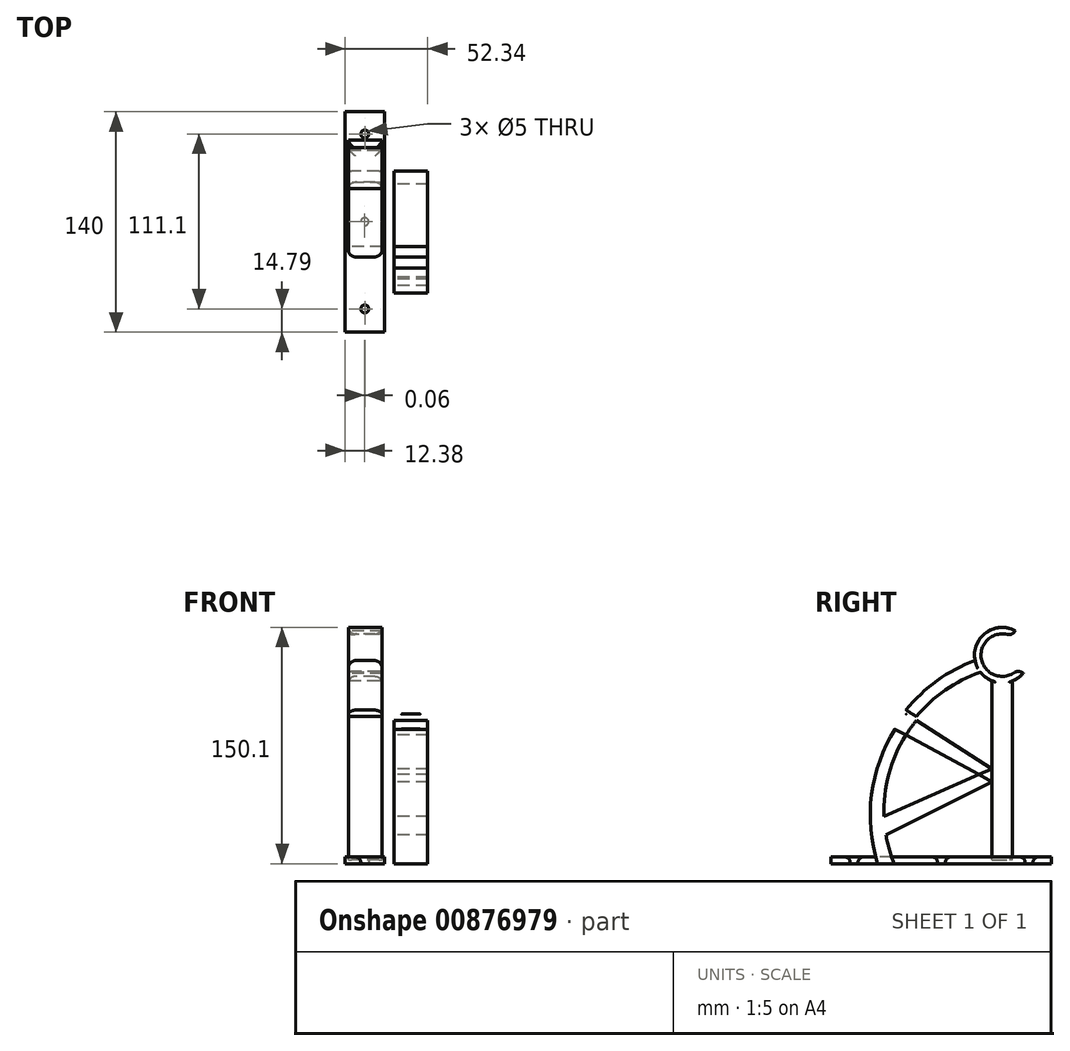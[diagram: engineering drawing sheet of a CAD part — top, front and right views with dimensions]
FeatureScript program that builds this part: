
annotation { "Feature Type Name" : "Feature", "Feature Type Description" : "" }
export const myFeature = defineFeature(function(context is Context, id is Id, definition is map)
    precondition{}
    {
        {
            var Q0;
            Q0=qCreatedBy(makeId("Top.planeOp"),FACE);
            var sketch = newSketch(context, id + "F0", { "sketchPlane" : qUnion([Q0])});
            skLineSegment(sketch, "E0.bottom", {"start": v(-31.04, 63.14) * mm, "end": v(-6.17, 63.14) * mm});
            skLineSegment(sketch, "E0.top", {"start": v(-31.04, -76.86) * mm, "end": v(-6.17, -76.86) * mm});
            skLineSegment(sketch, "E0.left", {"start": v(-31.04, 63.14) * mm, "end": v(-31.04, -76.86) * mm});
            skLineSegment(sketch, "E0.right", {"start": v(-6.17, 63.14) * mm, "end": v(-6.17, -76.86) * mm});
            skLineSegment(sketch, "E1", {"start": v(-18.6, 63.14) * mm, "end": v(-18.6, -76.86) * mm});
            skCircle(sketch, "E2", {"center": v(-18.6, 49.03) * mm, "radius": 2.5 * mm});
            skLineSegment(sketch, "E3.bottom", {"start": v(-27.13, 25.15) * mm, "end": v(-10.08, 25.15) * mm});
            skLineSegment(sketch, "E3.top", {"start": v(-27.13, 35.3) * mm, "end": v(-10.08, 35.3) * mm});
            skLineSegment(sketch, "E3.left", {"start": v(-27.13, 25.15) * mm, "end": v(-27.13, 35.3) * mm});
            skLineSegment(sketch, "E3.right", {"start": v(-10.08, 25.15) * mm, "end": v(-10.08, 35.3) * mm});
            skPoint(sketch, "E3.middle", {"position": v(-18.6, 30.23) * mm});
            skCircle(sketch, "E4", {"center": v(-18.6, -62.07) * mm, "radius": 2.5 * mm});
            skLineSegment(sketch, "E5.bottom", {"start": v(-27.13, -47.05) * mm, "end": v(-10.08, -47.05) * mm});
            skLineSegment(sketch, "E5.top", {"start": v(-27.13, -36.9) * mm, "end": v(-10.08, -36.9) * mm});
            skLineSegment(sketch, "E5.left", {"start": v(-27.13, -47.05) * mm, "end": v(-27.13, -36.9) * mm});
            skLineSegment(sketch, "E5.right", {"start": v(-10.08, -47.05) * mm, "end": v(-10.08, -36.9) * mm});
            skPoint(sketch, "E5.middle", {"position": v(-18.6, -41.97) * mm});
            skCircle(sketch, "E6", {"center": v(-18.66, -6.6) * mm, "radius": 2.5 * mm});
            skSolve(sketch);
        }
        {
            var Q0;
            Q0=qCreatedBy(makeId("Right.planeOp"),FACE);
            var sketch = newSketch(context, id + "F1", { "sketchPlane" : qUnion([Q0])});
            skLineSegment(sketch, "E7.bottom", {"start": v(25.47, 0) * mm, "end": v(38.53, 0) * mm});
            skLineSegment(sketch, "E7.top", {"start": v(25.47, 130) * mm, "end": v(38.53, 130) * mm});
            skLineSegment(sketch, "E7.left", {"start": v(25.47, 0) * mm, "end": v(25.47, 130) * mm});
            skLineSegment(sketch, "E7.right", {"start": v(38.53, 0) * mm, "end": v(38.53, 130) * mm});
            skArc(sketch, "E8", {"start": v(25.47, 130) * mm, "mid": v(-38.86, 80.66) * mm, "end": v(-47.12, 0) * mm});
            skArc(sketch, "E9", {"start": v(25.47, 121.23) * mm, "mid": v(-33.16, 74.74) * mm, "end": v(-36.67, 0) * mm});
            skLineSegment(sketch, "E10", {"start": v(-47.12, 0) * mm, "end": v(-36.67, 0) * mm});
            skPoint(sketch, "E11.centerSnap0", {"position": v(32, 130) * mm});
            skLineSegment(sketch, "E12.left", {"start": v(25.47, 52.07) * mm, "end": v(25.47, 60.27) * mm});
            skCircle(sketch, "E13", {"center": v(32, 130) * mm, "radius": 13.5 * mm});
            skCircle(sketch, "E14", {"center": v(32, 130) * mm, "radius": 17.6 * mm});
            skArc(sketch, "E15", {"start": v(57.75, 150.75) * mm, "mid": v(36, 132.31) * mm, "end": v(60.85, 118.33) * mm});
            skLineSegment(sketch, "E16", {"start": v(25.47, 52.07) * mm, "end": v(-50.48, 14.07) * mm});
            skLineSegment(sketch, "E17", {"start": v(-50.48, 14.07) * mm, "end": v(-51.75, 26.23) * mm});
            skLineSegment(sketch, "E18", {"start": v(-51.75, 26.23) * mm, "end": v(25.47, 60.27) * mm});
            skLineSegment(sketch, "E19", {"start": v(25.47, 52.07) * mm, "end": v(-36.03, 85.43) * mm});
            skLineSegment(sketch, "E20", {"start": v(-36.03, 85.43) * mm, "end": v(-29.09, 95.12) * mm});
            skLineSegment(sketch, "E21", {"start": v(-29.09, 95.12) * mm, "end": v(25.47, 60.27) * mm});
            skSolve(sketch);
        }
        {
            var Q0;
            {var subQ20=sQuery(id+"F0.wireOp",EDGE,"E0.left");Q0=makeQuery(id+"F0.imprint","IMPRINT",FACE,{"disambiguationData":[TD([[makeQuery(id+"F0.imprint","IMPRINT",EDGE,{"derivedFrom":subQ20}),1.0]])]});}
            var Q1;
            {var subQ13=sQuery(id+"F0.wireOp",EDGE,"E0.right");Q1=makeQuery(id+"F0.imprint","IMPRINT",FACE,{"disambiguationData":[TD([[makeQuery(id+"F0.imprint","IMPRINT",EDGE,{"derivedFrom":subQ13}),-1.0]])]});}
            var Q2;
            {var subQ5=sQuery(id+"F0.wireOp",EDGE,"E3.right");Q2=makeQuery(id+"F0.imprint","IMPRINT",FACE,{"disambiguationData":[TD([[makeQuery(id+"F0.imprint","IMPRINT",EDGE,{"derivedFrom":subQ5}),1.0]])]});}
            var Q3;
            {var subQ5=sQuery(id+"F0.wireOp",EDGE,"E3.left");Q3=makeQuery(id+"F0.imprint","IMPRINT",FACE,{"disambiguationData":[TD([[makeQuery(id+"F0.imprint","IMPRINT",EDGE,{"derivedFrom":subQ5}),-1.0]])]});}
            var Q4;
            {var subQ5=sQuery(id+"F0.wireOp",EDGE,"E5.left");Q4=makeQuery(id+"F0.imprint","IMPRINT",FACE,{"disambiguationData":[TD([[makeQuery(id+"F0.imprint","IMPRINT",EDGE,{"derivedFrom":subQ5}),-1.0]])]});}
            var Q5;
            {var subQ5=sQuery(id+"F0.wireOp",EDGE,"E5.right");Q5=makeQuery(id+"F0.imprint","IMPRINT",FACE,{"disambiguationData":[TD([[makeQuery(id+"F0.imprint","IMPRINT",EDGE,{"derivedFrom":subQ5}),1.0]])]});}
            extrude(context, id + "F2", {"entities" : qUnion([Q0, Q1, Q2, Q3, Q4, Q5]), "depth" : 4.3 * mm, "offsetDistance" : 25 * mm});
        }
        {
            var Q0;
            {var subQ0=sQuery(id+"F1.wireOp",EDGE,"E21");var subQ1=sQuery(id+"F1.wireOp",EDGE,"E9");var subQ2=makeQuery(id+"F1.imprint","INTERSECT",VERTEX,{"derivedFrom":[subQ1,subQ0]});Q0=makeQuery(id+"F1.imprint","IMPRINT",FACE,{"disambiguationData":[TD([[makeQuery(id+"F1.imprint","IMPRINT",EDGE,{"disambiguationData":[TD([[subQ2,-1.0]])],"derivedFrom":subQ1}),1.0]])]});}
            var Q1;
            {var subQ0=sQuery(id+"F1.wireOp",EDGE,"E16");var subQ1=sQuery(id+"F1.wireOp",EDGE,"E9");var subQ2=makeQuery(id+"F1.imprint","INTERSECT",VERTEX,{"derivedFrom":[subQ1,subQ0]});Q1=makeQuery(id+"F1.imprint","IMPRINT",FACE,{"disambiguationData":[TD([[makeQuery(id+"F1.imprint","IMPRINT",EDGE,{"disambiguationData":[TD([[subQ2,1.0]])],"derivedFrom":subQ1}),1.0]])]});}
            var Q2;
            {var subQ0=sQuery(id+"F1.wireOp",EDGE,"E12.left");Q2=makeQuery(id+"F1.imprint","IMPRINT",FACE,{"disambiguationData":[TD([[makeQuery(id+"F1.imprint","IMPRINT",EDGE,{"derivedFrom":subQ0}),1.0]])]});}
            var Q3;
            {var subQ6=sQuery(id+"F1.wireOp",EDGE,"E7.bottom");Q3=makeQuery(id+"F1.imprint","IMPRINT",FACE,{"disambiguationData":[TD([[makeQuery(id+"F1.imprint","IMPRINT",EDGE,{"derivedFrom":subQ6}),1.0]])]});}
            var Q4;
            {var subQ3=sQuery(id+"F1.wireOp",EDGE,"E19");var subQ5=sQuery(id+"F1.wireOp",EDGE,"E9");var subQ6=makeQuery(id+"F1.imprint","INTERSECT",VERTEX,{"derivedFrom":[subQ5,subQ3]});Q4=makeQuery(id+"F1.imprint","IMPRINT",FACE,{"disambiguationData":[TD([[makeQuery(id+"F1.imprint","IMPRINT",EDGE,{"disambiguationData":[TD([[subQ6,-1.0]])],"derivedFrom":subQ5}),-1.0]])]});}
            var Q5;
            {var subQ5=sQuery(id+"F1.wireOp",EDGE,"E17");Q5=makeQuery(id+"F1.imprint","IMPRINT",FACE,{"disambiguationData":[TD([[makeQuery(id+"F1.imprint","IMPRINT",EDGE,{"derivedFrom":subQ5}),-1.0]])]});}
            var Q6;
            {var subQ0=sQuery(id+"F1.wireOp",EDGE,"E10");Q6=makeQuery(id+"F1.imprint","IMPRINT",FACE,{"disambiguationData":[TD([[makeQuery(id+"F1.imprint","IMPRINT",EDGE,{"derivedFrom":subQ0}),1.0]])]});}
            var Q7;
            {var subQ5=sQuery(id+"F1.wireOp",EDGE,"E20");Q7=makeQuery(id+"F1.imprint","IMPRINT",FACE,{"disambiguationData":[TD([[makeQuery(id+"F1.imprint","IMPRINT",EDGE,{"derivedFrom":subQ5}),-1.0]])]});}
            var Q8;
            {var subQ3=sQuery(id+"F1.wireOp",EDGE,"E14");var subQ5=sQuery(id+"F1.wireOp",EDGE,"E9");var subQ6=makeQuery(id+"F1.imprint","INTERSECT",VERTEX,{"derivedFrom":[subQ5,subQ3]});Q8=makeQuery(id+"F1.imprint","IMPRINT",FACE,{"disambiguationData":[TD([[makeQuery(id+"F1.imprint","IMPRINT",EDGE,{"disambiguationData":[TD([[subQ6,-1.0]])],"derivedFrom":subQ5}),-1.0]])]});}
            var Q9;
            {var subQ0=sQuery(id+"F1.wireOp",EDGE,"E14");var subQ1=sQuery(id+"F1.wireOp",EDGE,"E8");var subQ2=makeQuery(id+"F1.imprint","INTERSECT",VERTEX,{"derivedFrom":[subQ1,subQ0]});Q9=makeQuery(id+"F1.imprint","IMPRINT",FACE,{"disambiguationData":[TD([[makeQuery(id+"F1.imprint","IMPRINT",EDGE,{"disambiguationData":[TD([[subQ2,1.0]])],"derivedFrom":subQ1}),1.0]])]});}
            var Q10;
            {var subQ0=sQuery(id+"F1.wireOp",EDGE,"E14");var subQ1=sQuery(id+"F1.wireOp",EDGE,"E7.left");var subQ2=makeQuery(id+"F1.imprint","INTERSECT",VERTEX,{"derivedFrom":[subQ1,subQ0]});Q10=makeQuery(id+"F1.imprint","IMPRINT",FACE,{"disambiguationData":[TD([[makeQuery(id+"F1.imprint","IMPRINT",EDGE,{"disambiguationData":[TD([[subQ2,-1.0]])],"derivedFrom":subQ1}),1.0]])]});}
            var Q11;
            {var subQ0=sQuery(id+"F1.wireOp",EDGE,"E14");var subQ1=sQuery(id+"F1.wireOp",EDGE,"E7.left");var subQ2=makeQuery(id+"F1.imprint","INTERSECT",VERTEX,{"derivedFrom":[subQ1,subQ0]});Q11=makeQuery(id+"F1.imprint","IMPRINT",FACE,{"disambiguationData":[TD([[makeQuery(id+"F1.imprint","IMPRINT",EDGE,{"disambiguationData":[TD([[subQ2,-1.0]])],"derivedFrom":subQ1}),-1.0]])]});}
            var Q12;
            {var subQ0=sQuery(id+"F1.wireOp",EDGE,"E14");var subQ1=sQuery(id+"F1.wireOp",EDGE,"E7.right");var subQ2=makeQuery(id+"F1.imprint","INTERSECT",VERTEX,{"derivedFrom":[subQ1,subQ0]});Q12=makeQuery(id+"F1.imprint","IMPRINT",FACE,{"disambiguationData":[TD([[makeQuery(id+"F1.imprint","IMPRINT",EDGE,{"disambiguationData":[TD([[subQ2,-1.0]])],"derivedFrom":subQ1}),-1.0]])]});}
            var Q13;
            {var subQ0=sQuery(id+"F1.wireOp",EDGE,"E14");var subQ1=sQuery(id+"F1.wireOp",EDGE,"E8");var subQ2=makeQuery(id+"F1.imprint","INTERSECT",VERTEX,{"derivedFrom":[subQ1,subQ0]});Q13=makeQuery(id+"F1.imprint","IMPRINT",FACE,{"disambiguationData":[TD([[makeQuery(id+"F1.imprint","IMPRINT",EDGE,{"disambiguationData":[TD([[subQ2,1.0]])],"derivedFrom":subQ1}),-1.0]])]});}
            extrude(context, id + "F3", {"entities" : qUnion([Q0, Q1, Q2, Q3, Q4, Q5, Q6, Q7, Q8, Q9, Q10, Q11, Q12, Q13]), "depth" : 21.3 * mm, "offsetDistance" : 25 * mm});
        }
        {
            var Q0;
            Q0=makeQuery(id+"F3.opExtrude","CAP_EDGE",EDGE,{"disambiguationData":[OSD([sQuery(id+"F1.wireOp",EDGE,"E7.right")])],"isStart":true});
            var Q1;
            {var subQ0=sQuery(id+"F1.wireOp",EDGE,"E7.left");Q1=makeQuery(id+"F3.opExtrude","CAP_EDGE",EDGE,{"disambiguationData":[OSD([subQ0]),TDD([makeQuery(id+"F1.imprint","IMPRINT",EDGE,{"disambiguationData":[TD([[makeQuery(id+"F1.imprint","INTERSECT",VERTEX,{"derivedFrom":[sQuery(id+"F1.wireOp",EDGE,"E7.bottom"),subQ0]}),-1.0]])],"derivedFrom":subQ0})])],"isStart":true});}
            var Q2;
            Q2=makeQuery(id+"F3.opExtrude","CAP_EDGE",EDGE,{"disambiguationData":[OSD([sQuery(id+"F1.wireOp",EDGE,"E7.right")])],"isStart":false});
            var Q3;
            {var subQ0=sQuery(id+"F1.wireOp",EDGE,"E7.left");Q3=makeQuery(id+"F3.opExtrude","CAP_EDGE",EDGE,{"disambiguationData":[OSD([subQ0]),TDD([makeQuery(id+"F1.imprint","IMPRINT",EDGE,{"disambiguationData":[TD([[makeQuery(id+"F1.imprint","INTERSECT",VERTEX,{"derivedFrom":[sQuery(id+"F1.wireOp",EDGE,"E7.bottom"),subQ0]}),-1.0]])],"derivedFrom":subQ0})])],"isStart":false});}
            var Q4;
            {var subQ0=sQuery(id+"F1.wireOp",EDGE,"E7.left");Q4=makeQuery(id+"F3.opExtrude","CAP_EDGE",EDGE,{"disambiguationData":[OSD([subQ0]),TDD([makeQuery(id+"F1.imprint","IMPRINT",EDGE,{"disambiguationData":[TD([[makeQuery(id+"F1.imprint","INTERSECT",VERTEX,{"derivedFrom":[subQ0,sQuery(id+"F1.wireOp",EDGE,"E14")]}),1.0]])],"derivedFrom":subQ0})])],"isStart":false});}
            var Q5;
            {var subQ0=sQuery(id+"F1.wireOp",EDGE,"E7.left");Q5=makeQuery(id+"F3.opExtrude","CAP_EDGE",EDGE,{"disambiguationData":[OSD([subQ0]),TDD([makeQuery(id+"F1.imprint","IMPRINT",EDGE,{"disambiguationData":[TD([[makeQuery(id+"F1.imprint","INTERSECT",VERTEX,{"derivedFrom":[subQ0,sQuery(id+"F1.wireOp",EDGE,"E14")]}),1.0]])],"derivedFrom":subQ0})])],"isStart":true});}
            fillet(context, id + "F4", {"entities" : qUnion([Q0, Q1, Q2, Q3, Q4, Q5]), "radius" : 1.93 * mm, "tangentPropagation" : true, "allowEdgeOverflow" : false});
        }
        {
            var Q0;
            Q0=makeQuery(id+"F2.opExtrude","CAP_EDGE",EDGE,{"disambiguationData":[OSD([sQuery(id+"F0.wireOp",EDGE,"E2")])],"isStart":false});
            var Q1;
            Q1=makeQuery(id+"F2.opExtrude","CAP_EDGE",EDGE,{"disambiguationData":[OSD([sQuery(id+"F0.wireOp",EDGE,"E6")])],"isStart":false});
            var Q2;
            Q2=makeQuery(id+"F2.opExtrude","CAP_EDGE",EDGE,{"disambiguationData":[OSD([sQuery(id+"F0.wireOp",EDGE,"E4")])],"isStart":false});
            fillet(context, id + "F5", {"entities" : qUnion([Q0, Q1, Q2]), "radius" : 3.5 * mm, "tangentPropagation" : true, "allowEdgeOverflow" : false});
        }
        {
            var Q0;
            {var subQ0=sQuery(id+"F1.wireOp",EDGE,"E8");Q0=makeQuery(id+"F3.opExtrude","CAP_EDGE",EDGE,{"disambiguationData":[OSD([subQ0]),TDD([makeQuery(id+"F1.imprint","IMPRINT",EDGE,{"disambiguationData":[TD([[makeQuery(id+"F1.imprint","INTERSECT",VERTEX,{"derivedFrom":[subQ0,sQuery(id+"F1.wireOp",EDGE,"E14")]}),-1.0]])],"derivedFrom":subQ0})])],"isStart":false});}
            var Q1;
            {var subQ0=sQuery(id+"F1.wireOp",EDGE,"E8");Q1=makeQuery(id+"F3.opExtrude","CAP_EDGE",EDGE,{"disambiguationData":[OSD([subQ0]),TDD([makeQuery(id+"F1.imprint","IMPRINT",EDGE,{"disambiguationData":[TD([[makeQuery(id+"F1.imprint","INTERSECT",VERTEX,{"derivedFrom":[subQ0,sQuery(id+"F1.wireOp",EDGE,"E14")]}),-1.0]])],"derivedFrom":subQ0})])],"isStart":true});}
            var Q2;
            {var subQ0=sQuery(id+"F1.wireOp",EDGE,"E8");Q2=makeQuery(id+"F3.opExtrude","CAP_EDGE",EDGE,{"disambiguationData":[OSD([subQ0]),TDD([makeQuery(id+"F1.imprint","IMPRINT",EDGE,{"disambiguationData":[TD([[makeQuery(id+"F1.imprint","INTERSECT",VERTEX,{"derivedFrom":[subQ0,sQuery(id+"F1.wireOp",EDGE,"E17"),sQuery(id+"F1.wireOp",EDGE,"E18")]}),1.0]])],"derivedFrom":subQ0})])],"isStart":true});}
            var Q3;
            {var subQ0=sQuery(id+"F1.wireOp",EDGE,"E8");Q3=makeQuery(id+"F3.opExtrude","CAP_EDGE",EDGE,{"disambiguationData":[OSD([subQ0]),TDD([makeQuery(id+"F1.imprint","IMPRINT",EDGE,{"disambiguationData":[TD([[makeQuery(id+"F1.imprint","INTERSECT",VERTEX,{"derivedFrom":[subQ0,sQuery(id+"F1.wireOp",EDGE,"E17"),sQuery(id+"F1.wireOp",EDGE,"E18")]}),1.0]])],"derivedFrom":subQ0})])],"isStart":false});}
            var Q4;
            Q4=makeQuery(id+"F3.opExtrude","CAP_EDGE",EDGE,{"disambiguationData":[OSD([sQuery(id+"F1.wireOp",EDGE,"E20")])],"isStart":false});
            var Q5;
            Q5=makeQuery(id+"F3.opExtrude","CAP_EDGE",EDGE,{"disambiguationData":[OSD([sQuery(id+"F1.wireOp",EDGE,"E20")])],"isStart":true});
            var Q6;
            Q6=makeQuery(id+"F3.opExtrude","CAP_EDGE",EDGE,{"disambiguationData":[OSD([sQuery(id+"F1.wireOp",EDGE,"E17")])],"isStart":false});
            var Q7;
            Q7=makeQuery(id+"F3.opExtrude","CAP_EDGE",EDGE,{"disambiguationData":[OSD([sQuery(id+"F1.wireOp",EDGE,"E17")])],"isStart":true});
            fillet(context, id + "F6", {"entities" : qUnion([Q0, Q1, Q2, Q3, Q4, Q5, Q6, Q7]), "radius" : 5 * mm, "tangentPropagation" : true, "allowEdgeOverflow" : false});
        }
        {
            var Q0;
            Q0=makeQuery(id+"F3.opExtrude","CAP_EDGE",EDGE,{"disambiguationData":[OSD([sQuery(id+"F1.wireOp",EDGE,"E13")])],"isStart":false});
            var Q1;
            Q1=makeQuery(id+"F3.opExtrude","CAP_EDGE",EDGE,{"disambiguationData":[OSD([sQuery(id+"F1.wireOp",EDGE,"E13")])],"isStart":true});
            var Q2;
            {var subQ0=sQuery(id+"F1.wireOp",EDGE,"E15");var subQ1=sQuery(id+"F1.wireOp",EDGE,"E13");Q2=makeQuery(id+"F3.opExtrude","SWEPT_EDGE",EDGE,{"disambiguationData":[OSD([subQ1,subQ0]),TDD([makeQuery(id+"F1.imprint","INTERSECT",VERTEX,{"disambiguationData":[OD(0.0)],"derivedFrom":[subQ1,subQ0]})])]});}
            var Q3;
            Q3=makeQuery(id+"F3.opExtrude","SWEPT_FACE",FACE,{"disambiguationData":[OSD([sQuery(id+"F1.wireOp",EDGE,"E13")])]});
            var Q4;
            {var subQ0=sQuery(id+"F1.wireOp",EDGE,"E15");var subQ1=sQuery(id+"F1.wireOp",EDGE,"E13");Q4=makeQuery(id+"F3.opExtrude","SWEPT_EDGE",EDGE,{"disambiguationData":[OSD([subQ1,subQ0]),TDD([makeQuery(id+"F1.imprint","INTERSECT",VERTEX,{"disambiguationData":[OD(1.0)],"derivedFrom":[subQ1,subQ0]})])]});}
            fillet(context, id + "F7", {"entities" : qUnion([Q0, Q1, Q2, Q3, Q4]), "radius" : 4.33 * mm, "tangentPropagation" : true, "allowEdgeOverflow" : false});
        }
        {
            var Q0;
            Q0=makeQuery(id+"F3.opExtrude","SWEPT_BODY",BODY,{"disambiguationData":[OSD([sQuery(id+"F1.wireOp",EDGE,"E7.bottom"),sQuery(id+"F1.wireOp",EDGE,"E7.left"),sQuery(id+"F1.wireOp",EDGE,"E7.right"),sQuery(id+"F1.wireOp",EDGE,"E8"),sQuery(id+"F1.wireOp",EDGE,"E9"),sQuery(id+"F1.wireOp",EDGE,"E10"),sQuery(id+"F1.wireOp",EDGE,"E13"),sQuery(id+"F1.wireOp",EDGE,"E14"),sQuery(id+"F1.wireOp",EDGE,"E15"),sQuery(id+"F1.wireOp",EDGE,"E16"),sQuery(id+"F1.wireOp",EDGE,"E17"),sQuery(id+"F1.wireOp",EDGE,"E18"),sQuery(id+"F1.wireOp",EDGE,"E19"),sQuery(id+"F1.wireOp",EDGE,"E20"),sQuery(id+"F1.wireOp",EDGE,"E21")])]});
            transform(context, id + "F8", {"entities" : qUnion([Q0]), "transformType" : TransformType.TRANSLATION_3D, "dx" : -29 * mm, "dy" : 0 * mm, "dz" : 2.5 * mm, "makeCopy" : false});
        }
    });
